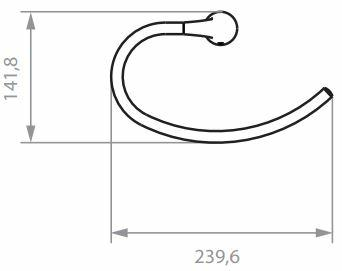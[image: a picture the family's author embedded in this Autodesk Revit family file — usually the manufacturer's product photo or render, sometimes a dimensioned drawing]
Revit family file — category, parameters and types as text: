
# Revit family: KR6030001_Toallero Argolla Koral
name_source: partatom
category: Furniture
units: mm (PartAtom-declared; Revit-internal decimal feet)

## family parameters
Always vertical = Yes
Cut with Voids When Loaded = No
Host = Wall
OmniClass Number = 23.31.25.25
OmniClass Title = Towel Bars
Room Calculation Point = No
Shared = No

## types (1)
- Niquel
    Alto = 1500 mm  [stored 4.92126 ft]
    Colección = Koral
    Creado por = BIMBAU
    Default Elevation = 0 mm  [stored 0 ft]
    Description = Ofrécele a tu baño funcionalidad y elegancia con el toallero argolla Koral, con sistema de fijación oculto. Combinable con las demás piezas de la línea Koral ¡Adquiérelo ahora!
    Fecha de creación = 07/04/2021
    Garantía = 30 años en estructura
    Garantía Acabados = 3 años en acabado
    Manufacturer = Corona
    Material = Corona_Cromado
    Referencia = KR6030001
    Resistencia = Resistente a la corrosión, pelado y decoloración por agua
    Temperatura de uso = De 4º C a 40º C (40º F y 104º F)
    URL = https://corona.co

note: [stored X ft] marks values corroborated as IEEE doubles in the binary element streams (Revit-internal decimal feet)

## geometry (parser evidence)
native form markers: Sweep x5
no freeform markers — native parametric forms only
